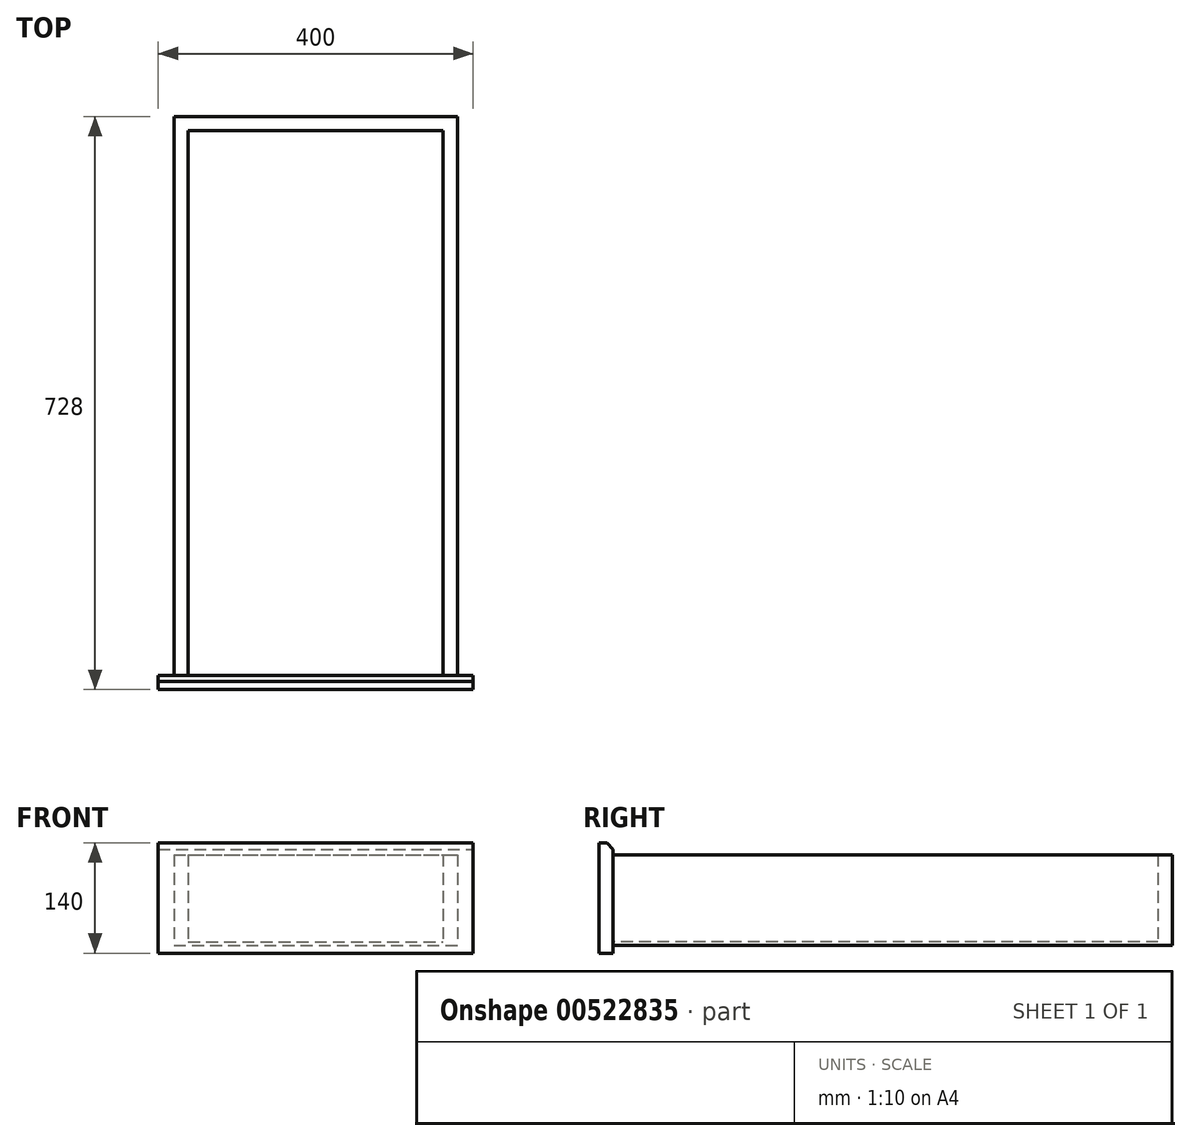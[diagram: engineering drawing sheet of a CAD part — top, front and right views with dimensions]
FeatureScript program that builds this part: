
annotation { "Feature Type Name" : "Feature", "Feature Type Description" : "" }
export const myFeature = defineFeature(function(context is Context, id is Id, definition is map)
    precondition{}
    {
        {
            var Q0;
            Q0=qCreatedBy(makeId("Top.planeOp"),FACE);
            var sketch = newSketch(context, id + "F0", { "sketchPlane" : qUnion([Q0])});
            skLineSegment(sketch, "E0.bottom", {"start": v(-180, 18) * mm, "end": v(-162, 18) * mm});
            skLineSegment(sketch, "E0.top", {"start": v(-180, 728) * mm, "end": v(-162, 728) * mm});
            skLineSegment(sketch, "E0.left", {"start": v(-180, 18) * mm, "end": v(-180, 728) * mm});
            skLineSegment(sketch, "E0.right", {"start": v(-162, 18) * mm, "end": v(-162, 728) * mm});
            skLineSegment(sketch, "E1.bottom", {"start": v(-162, 728) * mm, "end": v(162, 728) * mm});
            skLineSegment(sketch, "E1.top", {"start": v(-162, 710) * mm, "end": v(162, 710) * mm});
            skLineSegment(sketch, "E1.left", {"start": v(-162, 728) * mm, "end": v(-162, 710) * mm});
            skLineSegment(sketch, "E1.right", {"start": v(162, 728) * mm, "end": v(162, 710) * mm});
            skLineSegment(sketch, "E2.bottom", {"start": v(162, 728) * mm, "end": v(180, 728) * mm});
            skLineSegment(sketch, "E2.top", {"start": v(162, 18) * mm, "end": v(180, 18) * mm});
            skLineSegment(sketch, "E2.left", {"start": v(162, 728) * mm, "end": v(162, 18) * mm});
            skLineSegment(sketch, "E2.right", {"start": v(180, 728) * mm, "end": v(180, 18) * mm});
            skLineSegment(sketch, "E3.bottom", {"start": v(-200, 18) * mm, "end": v(200, 18) * mm});
            skLineSegment(sketch, "E3.top", {"start": v(-200, 0) * mm, "end": v(200, 0) * mm});
            skLineSegment(sketch, "E3.left", {"start": v(-200, 18) * mm, "end": v(-200, 0) * mm});
            skLineSegment(sketch, "E3.right", {"start": v(200, 18) * mm, "end": v(200, 0) * mm});
            skSolve(sketch);
        }
        {
            var Q0;
            {var subQ5=sQuery(id+"F0.wireOp",EDGE,"E2.bottom");Q0=makeQuery(id+"F0.imprint","IMPRINT",FACE,{"disambiguationData":[TD([[makeQuery(id+"F0.imprint","IMPRINT",EDGE,{"derivedFrom":subQ5}),-1.0]])]});}
            var Q1;
            {var subQ0=sQuery(id+"F0.wireOp",EDGE,"E1.bottom");Q1=makeQuery(id+"F0.imprint","IMPRINT",FACE,{"disambiguationData":[TD([[makeQuery(id+"F0.imprint","IMPRINT",EDGE,{"derivedFrom":subQ0}),-1.0]])]});}
            var Q2;
            Q2=makeQuery(id+"F0.imprint","IMPRINT",FACE,{"disambiguationData":[TD([[makeQuery(id+"F0.imprint","IMPRINT",EDGE,{"derivedFrom":sQuery(id+"F0.wireOp",EDGE,"E0.top")}),-1.0]])]});
            extrude(context, id + "F1", {"entities" : qUnion([Q0, Q1, Q2]), "depth" : 115 * mm, "offsetDistance" : 25 * mm});
        }
        {
            var Q0;
            Q0=makeQuery(id+"F0.imprint","IMPRINT",FACE,{"disambiguationData":[TD([[makeQuery(id+"F0.imprint","IMPRINT",EDGE,{"derivedFrom":sQuery(id+"F0.wireOp",EDGE,"E3.top")}),1.0]])]});
            extrude(context, id + "F2", {"entities" : qUnion([Q0]), "operationType" : NewBodyOperationType.ADD, "depth" : 130 * mm, "offsetDistance" : 25 * mm, "hasSecondDirection" : true, "secondDirectionOppositeDirection" : true, "secondDirectionDepth" : 10 * mm});
        }
        {
            var Q0;
            Q0=makeQuery(id+"F2.opExtrude","CAP_EDGE",EDGE,{"disambiguationData":[OSD([sQuery(id+"F0.wireOp",EDGE,"E3.bottom")])],"isStart":false});
            chamfer(context, id + "F3", {"entities" : qUnion([Q0]), "width" : 8 * mm, "tangentPropagation" : true});
        }
        {
            var Q0;
            {var subQ0=sQuery(id+"F0.wireOp",EDGE,"E0.right");Q0=makeQuery(id+"F0.imprint","IMPRINT",FACE,{"disambiguationData":[TD([[makeQuery(id+"F0.imprint","IMPRINT",EDGE,{"derivedFrom":subQ0}),-1.0]])]});}
            extrude(context, id + "F4", {"entities" : qUnion([Q0]), "operationType" : NewBodyOperationType.ADD, "depth" : 4 * mm, "offsetDistance" : 25 * mm});
        }
    });
